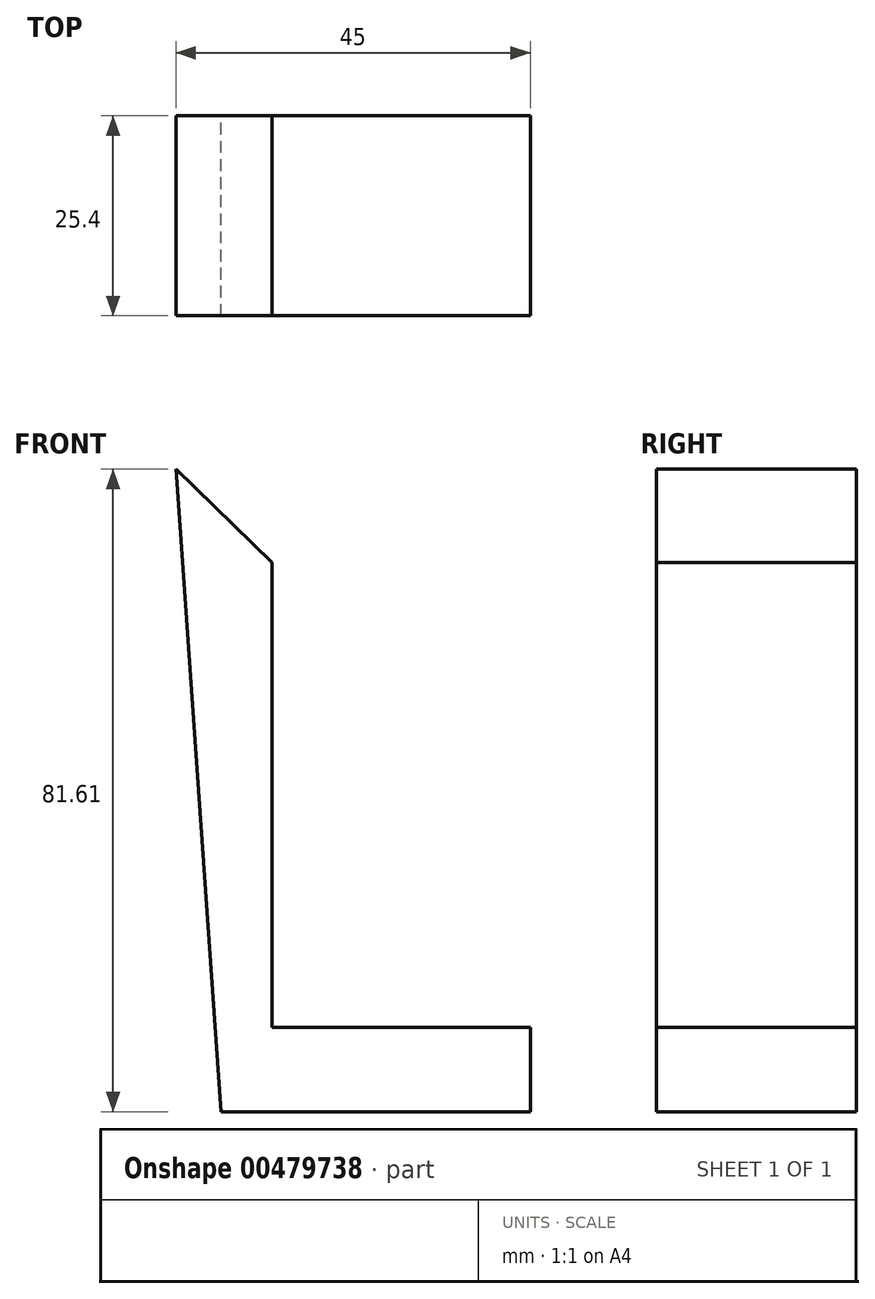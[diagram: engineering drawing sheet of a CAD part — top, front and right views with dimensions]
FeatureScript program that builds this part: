
annotation { "Feature Type Name" : "Feature", "Feature Type Description" : "" }
export const myFeature = defineFeature(function(context is Context, id is Id, definition is map)
    precondition{}
    {
        {
            var Q0;
            Q0=qCreatedBy(makeId("Front.planeOp"),FACE);
            var sketch = newSketch(context, id + "F0", { "sketchPlane" : qUnion([Q0])});
            skLineSegment(sketch, "E0", {"start": v(0, 0) * mm, "end": v(-32.8, 0) * mm});
            skLineSegment(sketch, "E1", {"start": v(-32.8, 0) * mm, "end": v(-32.8, 59.1) * mm});
            skLineSegment(sketch, "E2", {"start": v(-32.8, 59.1) * mm, "end": v(-45, 70.93) * mm});
            skLineSegment(sketch, "E3", {"start": v(-45, 70.93) * mm, "end": v(-39.28, -10.68) * mm});
            skLineSegment(sketch, "E4", {"start": v(-39.28, -10.68) * mm, "end": v(0, -10.68) * mm});
            skLineSegment(sketch, "E5", {"start": v(0, -10.68) * mm, "end": v(0, 0) * mm});
            skSolve(sketch);
        }
        {
            var Q0;
            Q0=makeQuery(id+"F0.imprint","IMPRINT",FACE,{"disambiguationData":[TD([[makeQuery(id+"F0.imprint","IMPRINT",EDGE,{"derivedFrom":sQuery(id+"F0.wireOp",EDGE,"E0")}),1.0]])]});
            extrude(context, id + "F1", {"entities" : qUnion([Q0]), "depth" : 25.4 * mm});
        }
    });
